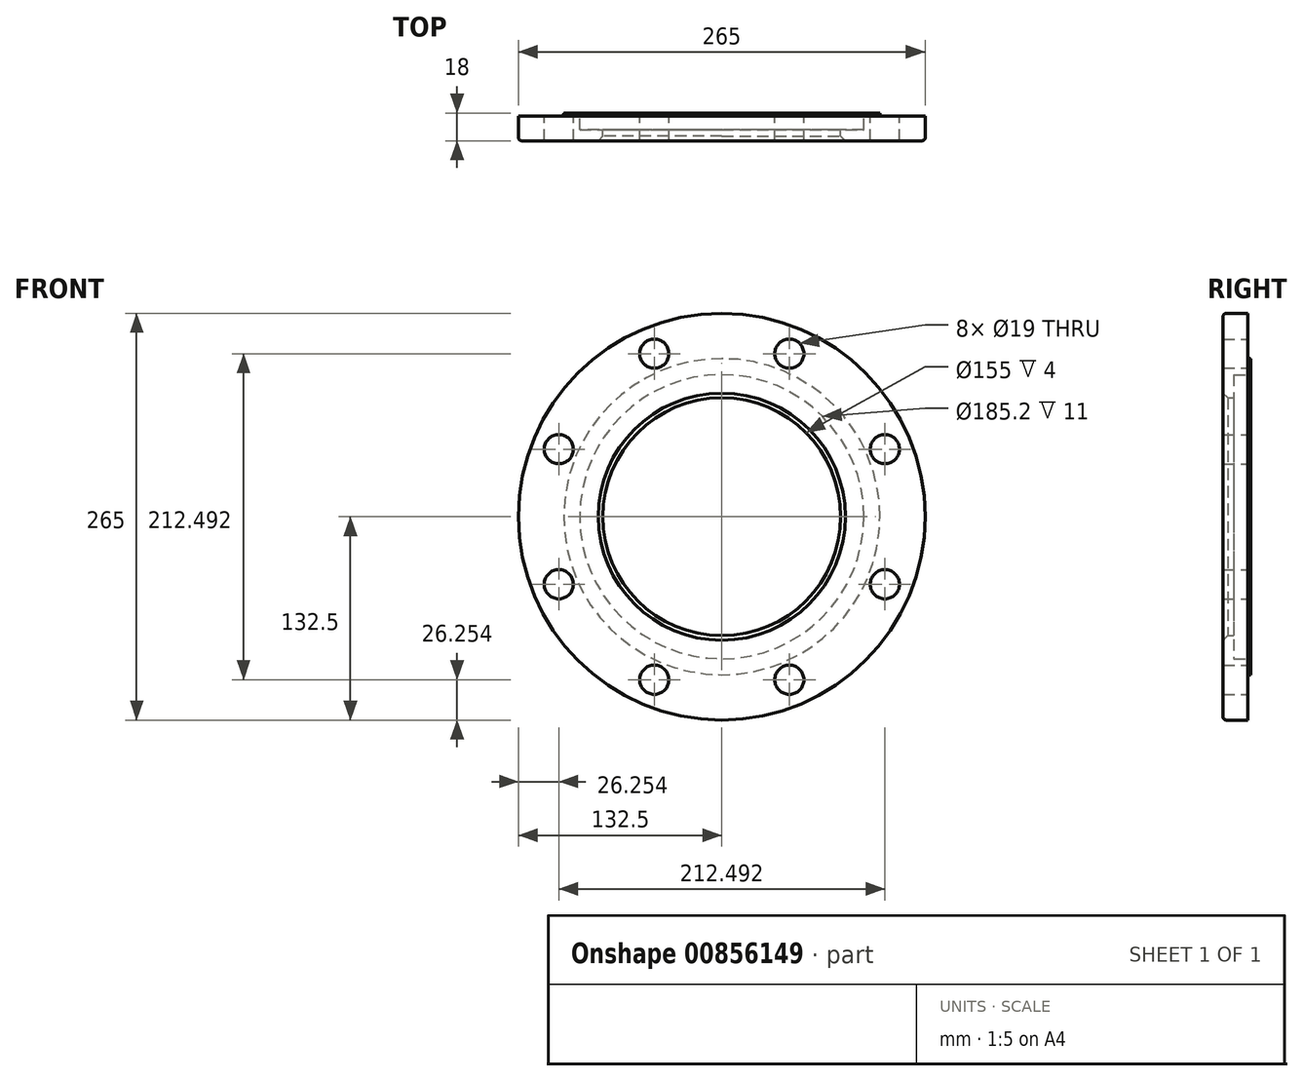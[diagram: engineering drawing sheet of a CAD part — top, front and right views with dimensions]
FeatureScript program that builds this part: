
annotation { "Feature Type Name" : "Feature", "Feature Type Description" : "" }
export const myFeature = defineFeature(function(context is Context, id is Id, definition is map)
    precondition{}
    {
        {
            var Q0;
            Q0=qCreatedBy(makeId("Front.planeOp"),FACE);
            var sketch = newSketch(context, id + "F0", { "sketchPlane" : qUnion([Q0])});
            skLineSegment(sketch, "E0", {"start": v(0, -526.54) * mm, "end": v(0, -90.52) * mm, "construction": true});
            skLineSegment(sketch, "E1", {"start": v(-10.08, -242) * mm, "end": v(258.14, -242) * mm, "construction": true});
            skLineSegment(sketch, "E2.0", {"start": v(-10.08, 0) * mm, "end": v(258.14, 0) * mm, "construction": true});
            skCircle(sketch, "E3", {"center": v(0, 0) * mm, "radius": 132.5 * mm});
            skCircle(sketch, "E4", {"center": v(0, 0) * mm, "radius": 115 * mm, "construction": true});
            skLineSegment(sketch, "E5", {"start": v(32.12, -13.3) * mm, "end": v(0, 0) * mm, "construction": true});
            skCircle(sketch, "E6", {"center": v(106.25, -44) * mm, "radius": 9.5 * mm});
            skCircle(sketch, "E7.1.0", {"center": v(106.25, 44) * mm, "radius": 9.5 * mm});
            skCircle(sketch, "E7.2.0", {"center": v(44, 106.25) * mm, "radius": 9.5 * mm});
            skCircle(sketch, "E7.3.0", {"center": v(-44, 106.25) * mm, "radius": 9.5 * mm});
            skCircle(sketch, "E7.4.0", {"center": v(-106.25, 44) * mm, "radius": 9.5 * mm});
            skCircle(sketch, "E7.5.0", {"center": v(-106.25, -44) * mm, "radius": 9.5 * mm});
            skCircle(sketch, "E7.6.0", {"center": v(-44, -106.25) * mm, "radius": 9.5 * mm});
            skCircle(sketch, "E7.7.0", {"center": v(44, -106.25) * mm, "radius": 9.5 * mm});
            skSolve(sketch);
        }
        {
            var Q0;
            Q0=makeQuery(id+"F0.imprint","IMPRINT",FACE,{"disambiguationData":[TD([[makeQuery(id+"F0.imprint","IMPRINT",EDGE,{"derivedFrom":sQuery(id+"F0.wireOp",EDGE,"E3")}),1.0]])]});
            extrude(context, id + "F1", {"entities" : qUnion([Q0]), "depth" : 18 * mm, "offsetDistance" : 25 * mm});
        }
        {
            var Q0;
            Q0=makeQuery(id+"F1.opExtrude","CAP_EDGE",EDGE,{"disambiguationData":[OSD([sQuery(id+"F0.wireOp",EDGE,"E3")])],"isStart":false});
            fillet(context, id + "F2", {"entities" : qUnion([Q0]), "radius" : 2 * mm, "tangentPropagation" : true, "allowEdgeOverflow" : false});
        }
        {
            var Q0;
            Q0=makeQuery(id+"F1.opExtrude","CAP_FACE",FACE,{"disambiguationData":[OSD([sQuery(id+"F0.wireOp",EDGE,"E3"),sQuery(id+"F0.wireOp",EDGE,"E6"),sQuery(id+"F0.wireOp",EDGE,"E7.1.0"),sQuery(id+"F0.wireOp",EDGE,"E7.2.0"),sQuery(id+"F0.wireOp",EDGE,"E7.3.0"),sQuery(id+"F0.wireOp",EDGE,"E7.4.0"),sQuery(id+"F0.wireOp",EDGE,"E7.5.0"),sQuery(id+"F0.wireOp",EDGE,"E7.6.0"),sQuery(id+"F0.wireOp",EDGE,"E7.7.0")])],"isStart":true});
            var sketch = newSketch(context, id + "F3", { "sketchPlane" : qUnion([Q0])});
            skCircle(sketch, "E8", {"center": v(0, 0) * mm, "radius": 103 * mm});
            skCircle(sketch, "E9", {"center": v(0, 0) * mm, "radius": 132.5 * mm});
            skSolve(sketch);
        }
        {
            var Q0;
            Q0=makeQuery(id+"F3.imprint","IMPRINT",FACE,{"disambiguationData":[TD([[makeQuery(id+"F3.imprint","IMPRINT",EDGE,{"derivedFrom":sQuery(id+"F3.wireOp",EDGE,"E8")}),-1.0]])]});
            extrude(context, id + "F4", {"entities" : qUnion([Q0]), "operationType" : NewBodyOperationType.REMOVE, "oppositeDirection" : true, "depth" : 2 * mm, "offsetDistance" : 25 * mm});
        }
        {
            var Q0;
            Q0=makeQuery(id+"F4.boolean.opBoolean","COPY",EDGE,{"derivedFrom":makeQuery(id+"F4.opExtrude","CAP_EDGE",EDGE,{"disambiguationData":[OSD([sQuery(id+"F3.wireOp",EDGE,"E8")])],"isStart":false})});
            fillet(context, id + "F5", {"entities" : qUnion([Q0]), "radius" : 2 * mm, "tangentPropagation" : true, "allowEdgeOverflow" : false});
        }
        {
            var Q0;
            Q0=makeQuery(id+"F1.opExtrude","CAP_FACE",FACE,{"disambiguationData":[OSD([sQuery(id+"F0.wireOp",EDGE,"E3"),sQuery(id+"F0.wireOp",EDGE,"E6"),sQuery(id+"F0.wireOp",EDGE,"E7.1.0"),sQuery(id+"F0.wireOp",EDGE,"E7.2.0"),sQuery(id+"F0.wireOp",EDGE,"E7.3.0"),sQuery(id+"F0.wireOp",EDGE,"E7.4.0"),sQuery(id+"F0.wireOp",EDGE,"E7.5.0"),sQuery(id+"F0.wireOp",EDGE,"E7.6.0"),sQuery(id+"F0.wireOp",EDGE,"E7.7.0")])],"isStart":true});
            var sketch = newSketch(context, id + "F6", { "sketchPlane" : qUnion([Q0])});
            skCircle(sketch, "E10", {"center": v(0, 0) * mm, "radius": 77.5 * mm});
            skCircle(sketch, "E11", {"center": v(0, 0) * mm, "radius": 92.6 * mm});
            skSolve(sketch);
        }
        {
            var Q0;
            Q0=makeQuery(id+"F6.imprint","IMPRINT",FACE,{"disambiguationData":[TD([[makeQuery(id+"F6.imprint","IMPRINT",EDGE,{"derivedFrom":sQuery(id+"F6.wireOp",EDGE,"E10")}),1.0]])]});
            extrude(context, id + "F7", {"entities" : qUnion([Q0]), "operationType" : NewBodyOperationType.REMOVE, "endBound" : BoundingType.THROUGH_ALL, "oppositeDirection" : true, "depth" : 25 * mm, "offsetDistance" : 25 * mm});
        }
        {
            var Q0;
            Q0=makeQuery(id+"F6.imprint","IMPRINT",FACE,{"disambiguationData":[TD([[makeQuery(id+"F6.imprint","IMPRINT",EDGE,{"derivedFrom":sQuery(id+"F6.wireOp",EDGE,"E10")}),-1.0]])]});
            extrude(context, id + "F8", {"entities" : qUnion([Q0]), "operationType" : NewBodyOperationType.REMOVE, "oppositeDirection" : true, "depth" : 11 * mm, "offsetDistance" : 25 * mm});
        }
        {
            var Q0;
            Q0=makeQuery(id+"F7.boolean.opBoolean","INTERSECT",EDGE,{"derivedFrom":[makeQuery(id+"F1.opExtrude","CAP_FACE",FACE,{"disambiguationData":[OSD([sQuery(id+"F0.wireOp",EDGE,"E3"),sQuery(id+"F0.wireOp",EDGE,"E6"),sQuery(id+"F0.wireOp",EDGE,"E7.1.0"),sQuery(id+"F0.wireOp",EDGE,"E7.2.0"),sQuery(id+"F0.wireOp",EDGE,"E7.3.0"),sQuery(id+"F0.wireOp",EDGE,"E7.4.0"),sQuery(id+"F0.wireOp",EDGE,"E7.5.0"),sQuery(id+"F0.wireOp",EDGE,"E7.6.0"),sQuery(id+"F0.wireOp",EDGE,"E7.7.0")])],"isStart":false}),makeQuery(id+"F7.opExtrude","SWEPT_FACE",FACE,{"disambiguationData":[OSD([sQuery(id+"F6.wireOp",EDGE,"E10")])]})]});
            chamfer(context, id + "F9", {"entities" : qUnion([Q0]), "width" : 3 * mm, "tangentPropagation" : true});
        }
    });
